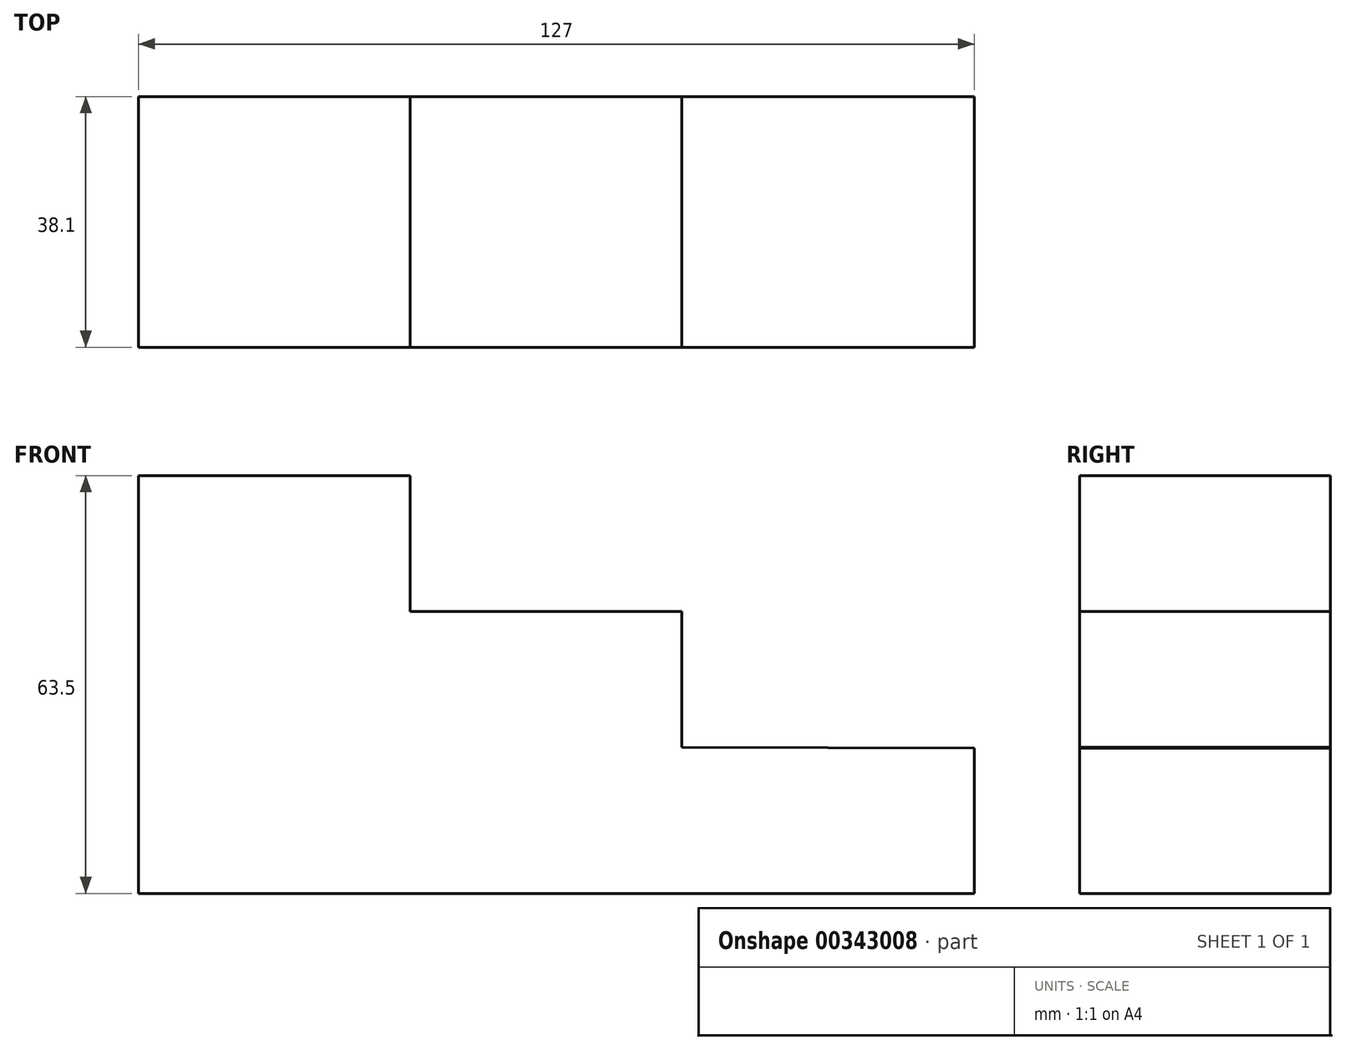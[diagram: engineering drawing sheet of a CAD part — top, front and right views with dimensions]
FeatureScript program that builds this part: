
annotation { "Feature Type Name" : "Feature", "Feature Type Description" : "" }
export const myFeature = defineFeature(function(context is Context, id is Id, definition is map)
    precondition{}
    {
        {
            var Q0;
            Q0=qCreatedBy(makeId("Front.planeOp"),FACE);
            var sketch = newSketch(context, id + "F0", { "sketchPlane" : qUnion([Q0])});
            skLineSegment(sketch, "E0", {"start": v(-71.53, -13.62) * mm, "end": v(55.47, -13.62) * mm});
            skLineSegment(sketch, "E1", {"start": v(-71.53, -13.62) * mm, "end": v(-71.53, 49.88) * mm});
            skLineSegment(sketch, "E2", {"start": v(-71.53, 49.88) * mm, "end": v(-30.26, 49.88) * mm});
            skLineSegment(sketch, "E3", {"start": v(-30.26, 49.88) * mm, "end": v(-30.26, 29.23) * mm});
            skLineSegment(sketch, "E4", {"start": v(-30.26, 29.23) * mm, "end": v(11.02, 29.23) * mm});
            skLineSegment(sketch, "E5", {"start": v(11.02, 29.23) * mm, "end": v(11.02, 8.58) * mm});
            skLineSegment(sketch, "E6", {"start": v(55.47, -13.62) * mm, "end": v(55.47, 8.44) * mm});
            skLineSegment(sketch, "E7", {"start": v(11.02, 8.58) * mm, "end": v(55.47, 8.44) * mm});
            skSolve(sketch);
        }
        {
            var Q0;
            Q0=makeQuery(id+"F0.imprint","IMPRINT",FACE,{"disambiguationData":[TD([[makeQuery(id+"F0.imprint","IMPRINT",EDGE,{"derivedFrom":sQuery(id+"F0.wireOp",EDGE,"E0")}),1.0]])]});
            extrude(context, id + "F1", {"entities" : qUnion([Q0]), "depth" : 38.1 * mm});
        }
    });
